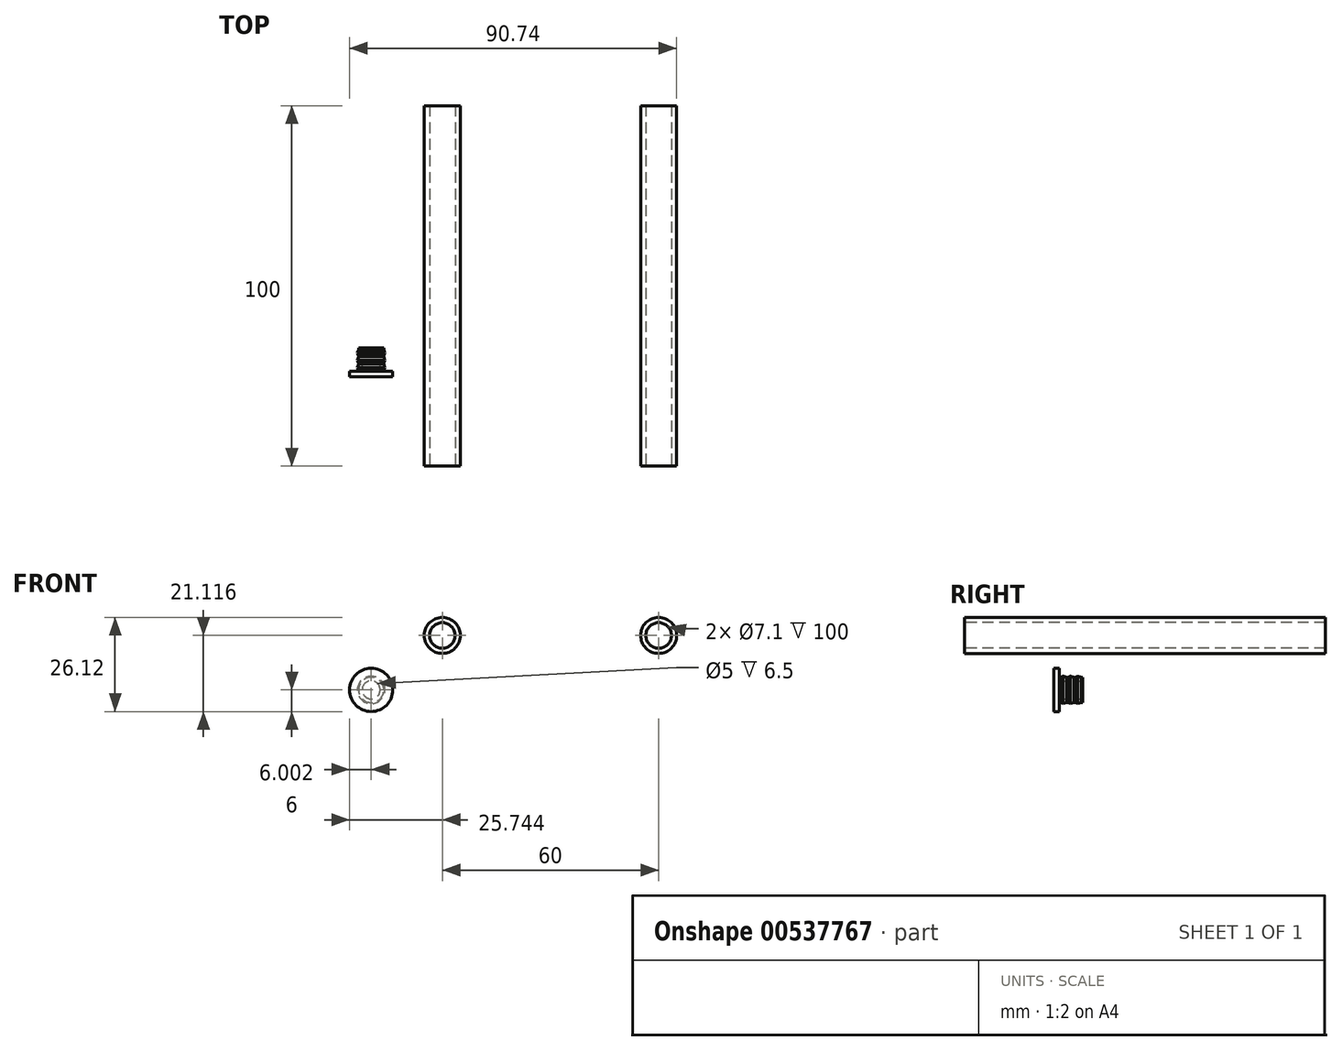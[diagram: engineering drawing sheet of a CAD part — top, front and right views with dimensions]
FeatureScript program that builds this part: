
annotation { "Feature Type Name" : "Feature", "Feature Type Description" : "" }
export const myFeature = defineFeature(function(context is Context, id is Id, definition is map)
    precondition{}
    {
        {
            var Q0;
            Q0=qCreatedBy(makeId("Front.planeOp"),FACE);
            var sketch = newSketch(context, id + "F0", { "sketchPlane" : qUnion([Q0])});
            skCircle(sketch, "E0", {"center": v(-26.9, 15.12) * mm, "radius": 5 * mm});
            skCircle(sketch, "E1.0", {"center": v(-26.9, 15.12) * mm, "radius": 3.55 * mm});
            skCircle(sketch, "E2", {"center": v(33.1, 15.12) * mm, "radius": 5 * mm});
            skCircle(sketch, "E3.0", {"center": v(33.1, 15.12) * mm, "radius": 3.55 * mm});
            skSolve(sketch);
        }
        {
            var Q0;
            Q0=makeQuery(id+"F0.imprint","IMPRINT",FACE,{"disambiguationData":[TD([[makeQuery(id+"F0.imprint","IMPRINT",EDGE,{"derivedFrom":sQuery(id+"F0.wireOp",EDGE,"E0")}),1.0]])]});
            var Q1;
            Q1=makeQuery(id+"F0.imprint","IMPRINT",FACE,{"disambiguationData":[TD([[makeQuery(id+"F0.imprint","IMPRINT",EDGE,{"derivedFrom":sQuery(id+"F0.wireOp",EDGE,"E2")}),1.0]])]});
            extrude(context, id + "F1", {"entities" : qUnion([Q0, Q1]), "endBound" : BoundingType.SYMMETRIC, "oppositeDirection" : true, "depth" : 100 * mm, "offsetDistance" : 25 * mm});
        }
        {
            var Q0;
            Q0=qCreatedBy(makeId("Top.planeOp"),FACE);
            var sketch = newSketch(context, id + "F2", { "sketchPlane" : qUnion([Q0])});
            skLineSegment(sketch, "E4.bottom", {"start": v(-52.65, -23.72) * mm, "end": v(-46.65, -23.72) * mm});
            skLineSegment(sketch, "E4.top", {"start": v(-52.65, -25.22) * mm, "end": v(-46.65, -25.22) * mm});
            skLineSegment(sketch, "E4.left", {"start": v(-52.65, -23.72) * mm, "end": v(-52.65, -25.22) * mm});
            skLineSegment(sketch, "E4.right", {"start": v(-46.65, -23.72) * mm, "end": v(-46.65, -25.22) * mm});
            skLineSegment(sketch, "E5", {"start": v(-50.15, -23.72) * mm, "end": v(-50.15, -23.27) * mm});
            skLineSegment(sketch, "E6", {"start": v(-50.15, -23.27) * mm, "end": v(-50.45, -22.67) * mm});
            skLineSegment(sketch, "E7", {"start": v(-50.45, -22.67) * mm, "end": v(-50.15, -21.7) * mm});
            skLineSegment(sketch, "E8", {"start": v(-50.15, -21.7) * mm, "end": v(-50.15, -21.25) * mm});
            skLineSegment(sketch, "E9", {"start": v(-50.15, -21.25) * mm, "end": v(-50.45, -20.65) * mm});
            skLineSegment(sketch, "E10", {"start": v(-50.45, -20.65) * mm, "end": v(-50.15, -19.68) * mm});
            skLineSegment(sketch, "E11", {"start": v(-50.15, -19.68) * mm, "end": v(-50.15, -19.23) * mm});
            skLineSegment(sketch, "E12", {"start": v(-50.15, -19.23) * mm, "end": v(-50.45, -18.64) * mm});
            skLineSegment(sketch, "E13", {"start": v(-50.45, -18.64) * mm, "end": v(-50.15, -17.67) * mm});
            skLineSegment(sketch, "E14", {"start": v(-50.15, -17.67) * mm, "end": v(-50.15, -17.22) * mm});
            skLineSegment(sketch, "E15", {"start": v(-50.15, -17.22) * mm, "end": v(-49.15, -17.22) * mm});
            skLineSegment(sketch, "E16", {"start": v(-49.15, -17.22) * mm, "end": v(-49.15, -23.72) * mm});
            skSolve(sketch);
        }
        {
            var Q0;
            Q0 = qSketchRegion(id + "F2", true);
            var Q1;
            Q1=sQuery(id+"F2.wireOp",EDGE,"E4.right");
            revolve(context, id + "F3", {"entities" : qUnion([Q0]), "axis" : qUnion([Q1]), "revolveType" : RevolveType.FULL});
        }
    });
